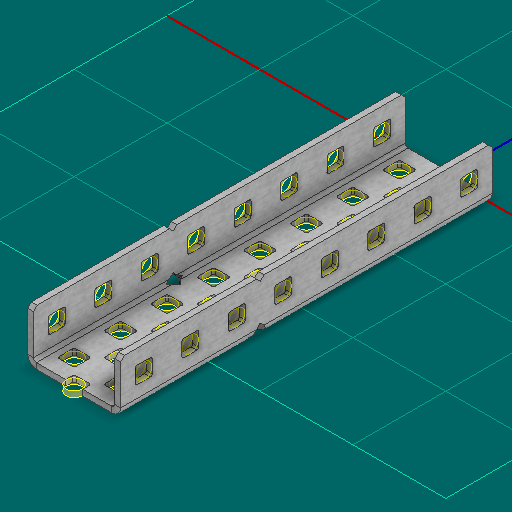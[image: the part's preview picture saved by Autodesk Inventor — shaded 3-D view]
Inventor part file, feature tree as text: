
AUTODESK INVENTOR PART (.ipt)
format: ipt  version: 2025 (Build 290162000, 162)  size: 866,304 bytes
history: native  units: in
note: dims shown in document units (in); Inventor stores cm internally (conversion verified against a paired STEP export)
features: other x86, sketch x5, sheet_metal_op x1
ambient origin geometry x8: Origin, YZ Plane, XZ Plane, XY Plane, X Axis, Y Axis, Z Axis, Center Point
bodies: Solid1 (feature_tree)
feature tree (92):
  other  "Alu C 1x2x1x8.ipt"
  other  "Solid1::Alu C 1x2x1x8.ipt"
  other  "TaggingFeature1"
  sketch  "Sketch1"  dims[d0=0.3937in]
  sketch  "Sketch2"  dims[d1=0.0625in]
  sketch  "Sketch3"
  other  "Flange Pattern Sketch"
  sketch  "Sketch9"
  sheet_metal_op  "Body Pattern Sketch"
  other  "Arc Length"
  sketch  "Sketch14"
  other  "Flange Pattern Plane"
  other  "Srf1"
  other  "Srf2"
  other  "Srf3"
  other  "Srf4"
  other  "Srf5"
  other  "Srf6"
  other  "Srf7"
  other  "Srf8"
  other  "Srf9"
  other  "Srf10"
  other  "Srf11"
  other  "Srf12"
  other  "Srf13"
  other  "Srf14"
  other  "Srf15"
  other  "Srf16"
  other  "Srf17"
  other  "Srf18"
  other  "Srf19"
  other  "Srf20"
  other  "Srf21"
  other  "Srf22"
  other  "Srf23"
  other  "Srf24"
  other  "Srf25"
  other  "Srf26"
  other  "Srf27"
  other  "Srf28"
  other  "Srf29"
  other  "Srf30"
  other  "Srf31"
  other  "Srf32"
  other  "Srf33"
  other  "Srf34"
  other  "Srf35"
  other  "Srf36"
  other  "Srf37"
  other  "Srf38"
  other  "Srf39"
  other  "Srf40"
  other  "Srf1::Derived"
  other  "Srf2::Derived"
  other  "Srf823::Derived"
  other  "Srf824::Derived"
  other  "Srf825::Derived"
  other  "Srf826::Derived"
  other  "Srf827::Derived"
  other  "Srf828::Derived"
  other  "Srf829::Derived"
  other  "Srf922::Derived"
  other  "Srf923::Derived"
  other  "Srf924::Derived"
  other  "Srf925::Derived"
  other  "Srf926::Derived"
  other  "Srf1143::Derived"
  other  "Srf1144::Derived"
  other  "Srf91::Derived"
  other  "Srf92::Derived"
  other  "Srf856::Derived"
  other  "Srf857::Derived"
  other  "Srf858::Derived"
  other  "Srf859::Derived"
  other  "Srf860::Derived"
  other  "Srf861::Derived"
  other  "Srf862::Derived"
  other  "Srf959::Derived"
  other  "Srf960::Derived"
  other  "Srf961::Derived"
  other  "Srf962::Derived"
  other  "Srf963::Derived"
  other  "Srf1199::Derived"
  other  "Srf1200::Derived"
  other  "Srf786::Derived"
  other  "Srf889::Derived"
  other  "Srf890::Derived"
  other  "Srf891::Derived"
  other  "Srf892::Derived"
  other  "Srf893::Derived"
  other  "Srf894::Derived"
  other  "Srf895::Derived"
